# Revit family: BVN_BSKF
name_source: partatom
category: Mechanical Equipment
units: mm (PartAtom-declared; Revit-internal decimal feet)

## family parameters
Always vertical = Yes
Cut with Voids When Loaded = No
OmniClass Number = 23.75.00.00
OmniClass Title = Climate Control (HVAC)
Part Type = Breaks Into
Room Calculation Point = No
Round Connector Dimension = Use Diameter
Shared = No
Work Plane-Based = No

## types (5) — shared parameters
Description = Duct Fan
Frequency = 50 Hz
Insulation Class = F
Manufacturer = Bahçıvan Elektrik Motor San. ve Tic. Ltd. Şti.
Material = <By Category>
Model = BSKF
Protection Class = 44
Sac = -2 mm  [stored -0.00656168 ft]
URL = http://www.bahcivanmotor.com.tr

## per-type parameters (varying)
| type | A | Air Flow | B | C | Capacitor | Corners | Current | D | E | F | G | Power | Sound Pressure Level dB(A) | Speed ( d/d ) | Voltage | Weight |
| BSKF 40-20 | 200 mm  [stored 0.656168 ft] | 990.0 m³/h | 400 mm  [stored 1.31234 ft] | 502 mm  [stored 1.64698 ft] | 6 | 15 mm  [stored 0.0492126 ft] | 1 A | 415 mm  [stored 1.36155 ft] | 215 mm | 440 mm  [stored 1.44357 ft] | 240 mm  [stored 0.787402 ft] | 315 W | 53 | 1590 | 230 V | 14.00 kg |
| BSKF 50-25 | 250 mm  [stored 0.82021 ft] | 1750.0 m³/h | 500 mm  [stored 1.64042 ft] | 532 mm  [stored 1.74541 ft] | 10 | 20 mm  [stored 0.0656168 ft] | 3 A | 515 mm  [stored 1.68963 ft] | 260 mm  [stored 0.853018 ft] | 540 mm  [stored 1.77165 ft] | 290 mm  [stored 0.951444 ft] | 635 W | 55 | 1300 | 230 V | 19.00 kg |
| BSKF 60-30 | 300 mm | 2950.0 m³/h | 600 mm | 642 mm  [stored 2.1063 ft] | 0 | 20 mm  [stored 0.0656168 ft] | 2 A | 615 mm  [stored 2.01772 ft] | 310 mm  [stored 1.01706 ft] | 640 mm  [stored 2.09974 ft] | 340 mm  [stored 1.11549 ft] | 1335 W | 60 | 1200 | 380 V | 36.00 kg |
| BSKF 60-35 | 350 mm  [stored 1.14829 ft] | 4250.0 m³/h | 600 mm | 720 mm  [stored 2.3622 ft] | 0 | 20 mm  [stored 0.0656168 ft] | 3 A | 615 mm  [stored 2.01772 ft] | 360 mm  [stored 1.1811 ft] | 650 mm  [stored 2.13255 ft] | 390 mm  [stored 1.27953 ft] | 1755 W | 62 | 1200 | 380 V | 44.00 kg |
| BSKF 50-30 | 300 mm | 2100.0 m³/h | 500 mm  [stored 1.64042 ft] | 562 mm  [stored 1.84383 ft] | 10 | 20 mm  [stored 0.0656168 ft] | 3 A | 515 mm  [stored 1.68963 ft] | 310 mm  [stored 1.01706 ft] | 540 mm  [stored 1.77165 ft] | 340 mm  [stored 1.11549 ft] | 675 W | 58 | 1300 | 230 V | 23.00 kg |

note: [stored X ft] marks values corroborated as IEEE doubles in the binary element streams (Revit-internal decimal feet)

## geometry (parser evidence)
native form markers: Sweep x2
no freeform markers — native parametric forms only
